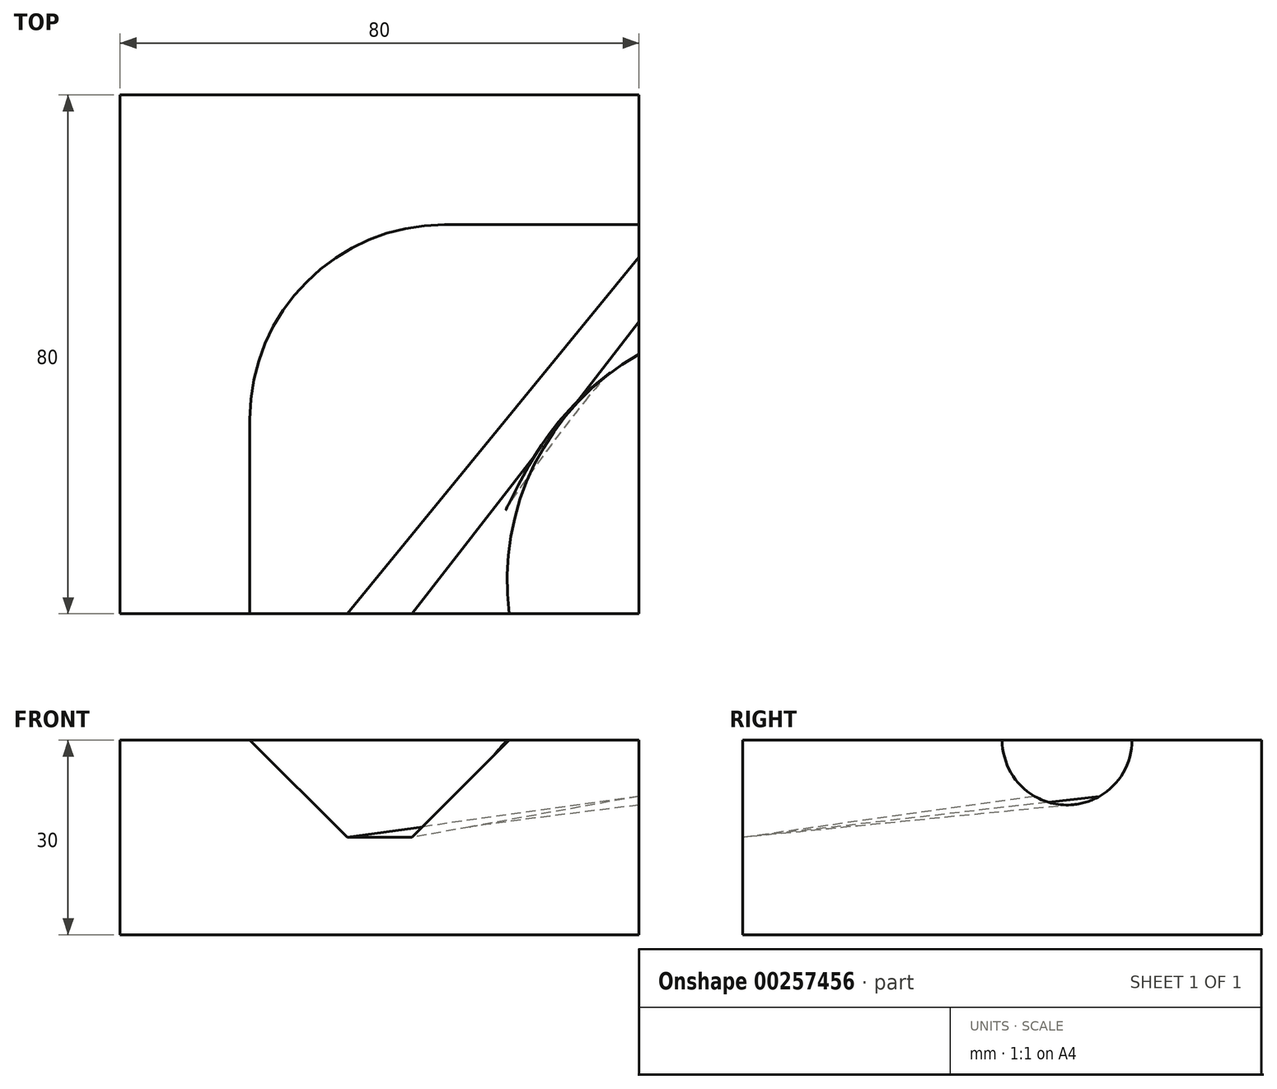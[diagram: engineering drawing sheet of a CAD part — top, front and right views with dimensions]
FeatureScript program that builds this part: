
annotation { "Feature Type Name" : "Feature", "Feature Type Description" : "" }
export const myFeature = defineFeature(function(context is Context, id is Id, definition is map)
    precondition{}
    {
        {
            var Q0;
            Q0=qCreatedBy(makeId("Top.planeOp"),FACE);
            var sketch = newSketch(context, id + "F0", { "sketchPlane" : qUnion([Q0])});
            skLineSegment(sketch, "E0.bottom", {"start": v(-40, 40) * mm, "end": v(40, 40) * mm});
            skLineSegment(sketch, "E0.top", {"start": v(-40, -40) * mm, "end": v(40, -40) * mm});
            skLineSegment(sketch, "E0.left", {"start": v(-40, 40) * mm, "end": v(-40, -40) * mm});
            skLineSegment(sketch, "E0.right", {"start": v(40, 40) * mm, "end": v(40, -40) * mm});
            skPoint(sketch, "E0.middle", {"position": v(0, 0) * mm});
            skArc(sketch, "E1", {"start": v(40, 0) * mm, "mid": v(23.89, -16.94) * mm, "end": v(20, -40) * mm});
            skLineSegment(sketch, "E2", {"start": v(-20, -10) * mm, "end": v(-20, -40) * mm});
            skLineSegment(sketch, "E3", {"start": v(10, 20) * mm, "end": v(40, 20) * mm});
            skArc(sketch, "E4", {"start": v(10, 20) * mm, "mid": v(-11.21, 11.21) * mm, "end": v(-20, -10) * mm});
            skSolve(sketch);
        }
        {
            var Q0;
            {var subQ1=sQuery(id+"F0.wireOp",EDGE,"E0.bottom");Q0=makeQuery(id+"F0.imprint","IMPRINT",FACE,{"disambiguationData":[TD([[makeQuery(id+"F0.imprint","IMPRINT",EDGE,{"derivedFrom":subQ1}),-1.0]])]});}
            var Q1;
            {var subQ1=sQuery(id+"F0.wireOp",EDGE,"E1");Q1=makeQuery(id+"F0.imprint","IMPRINT",FACE,{"disambiguationData":[TD([[makeQuery(id+"F0.imprint","IMPRINT",EDGE,{"derivedFrom":subQ1}),-1.0]])]});}
            var Q2;
            {var subQ3=sQuery(id+"F0.wireOp",EDGE,"E1");Q2=makeQuery(id+"F0.imprint","IMPRINT",FACE,{"disambiguationData":[TD([[makeQuery(id+"F0.imprint","IMPRINT",EDGE,{"derivedFrom":subQ3}),1.0]])]});}
            extrude(context, id + "F1", {"entities" : qUnion([Q0, Q1, Q2]), "oppositeDirection" : true, "depth" : 30 * mm});
        }
        {
            var Q0;
            Q0=makeQuery(id+"F1.opExtrude","SWEPT_FACE",FACE,{"disambiguationData":[OSD([sQuery(id+"F0.wireOp",EDGE,"E0.top")])]});
            var sketch = newSketch(context, id + "F2", { "sketchPlane" : qUnion([Q0])});
            skPoint(sketch, "E5.0", {"position": v(-20, 0) * mm});
            skPoint(sketch, "E6.0", {"position": v(20, 0) * mm});
            skLineSegment(sketch, "E7", {"start": v(-20, 0) * mm, "end": v(-5, -15) * mm});
            skLineSegment(sketch, "E8", {"start": v(-5, -15) * mm, "end": v(5, -15) * mm});
            skLineSegment(sketch, "E9", {"start": v(5, -15) * mm, "end": v(20, 0) * mm});
            skSolve(sketch);
        }
        {
            var Q0;
            Q0=makeQuery(id+"F1.opExtrude","SWEPT_FACE",FACE,{"disambiguationData":[OSD([sQuery(id+"F0.wireOp",EDGE,"E0.right")])]});
            var sketch = newSketch(context, id + "F3", { "sketchPlane" : qUnion([Q0])});
            skPoint(sketch, "E10.0", {"position": v(0, 0) * mm});
            skPoint(sketch, "E11.0", {"position": v(20, 0) * mm});
            skArc(sketch, "E12", {"start": v(0, 0) * mm, "mid": v(10, -10) * mm, "end": v(20, 0) * mm});
            skSolve(sketch);
        }
        {
            var Q0;
            {var subQ1=sQuery(id+"F0.wireOp",EDGE,"E0.bottom");Q0=makeQuery(id+"F0.imprint","IMPRINT",FACE,{"disambiguationData":[TD([[makeQuery(id+"F0.imprint","IMPRINT",EDGE,{"derivedFrom":subQ1}),-1.0]])]});}
            var sketch = newSketch(context, id + "F4", { "sketchPlane" : qUnion([Q0])});
            skLineSegment(sketch, "E13.0", {"start": v(-20, -10) * mm, "end": v(-20, -40) * mm});
            skArc(sketch, "E14.0", {"start": v(10, 20) * mm, "mid": v(-11.21, 11.21) * mm, "end": v(-20, -10) * mm});
            skLineSegment(sketch, "E15.0", {"start": v(10, 20) * mm, "end": v(40, 20) * mm});
            skSolve(sketch);
        }
        {
            var Q1;
            {var subQ0=sQuery(id+"F3.wireOp",EDGE,"E12");Q1=makeQuery(id+"F3.imprint","IMPRINT",FACE,{"disambiguationData":[TD([[makeQuery(id+"F3.imprint","IMPRINT",EDGE,{"derivedFrom":subQ0}),1.0]])]});}
            var Q2;
            {var subQ0=sQuery(id+"F2.wireOp",EDGE,"E7");Q2=makeQuery(id+"F2.imprint","IMPRINT",FACE,{"disambiguationData":[TD([[makeQuery(id+"F2.imprint","IMPRINT",EDGE,{"derivedFrom":subQ0}),1.0]])]});}
            var Q3;
            Q3=sQuery(id+"F0.wireOp",EDGE,"E1");
            var Q4;
            Q4 = qConstructionFilter(qBodyType(qCreatedBy(id + "F4" ,EDGE), BodyType.WIRE), ConstructionObject.NO);
            loft(context, id + "F5", {"operationType" : NewBodyOperationType.REMOVE, "addGuides" : true, "sheetProfilesArray" : [{ "sheetProfileEntities" : qUnion([Q1]) }, { "sheetProfileEntities" : qUnion([Q2]) }], "guidesArray" : [{ "guideEntities" : qUnion([Q3]), "guideDerivativeType" : LoftGuideDerivativeType.DEFAULT, "guideDerivativeMagnitude" : 1 }, { "guideEntities" : qUnion([Q4]), "guideDerivativeType" : LoftGuideDerivativeType.DEFAULT, "guideDerivativeMagnitude" : 1 }]});
        }
    });
